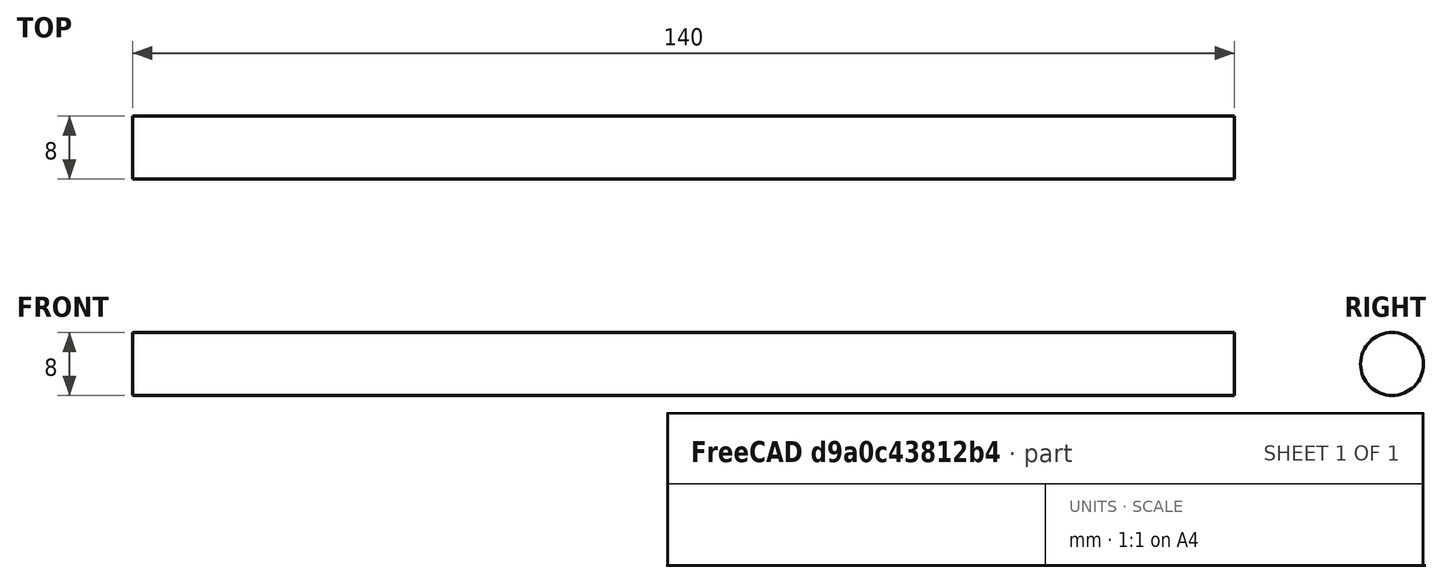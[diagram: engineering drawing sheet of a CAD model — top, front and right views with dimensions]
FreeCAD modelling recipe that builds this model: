
FCSTD DOCUMENT  (FreeCAD 0.15R4671 (Git))
Label: axe 2
License: All rights reserved
LicenseURL: http://fr.wikipedia.org/wiki/<copyright redacted>
objects: Sketcher::SketchObject×1, PartDesign::Revolution×1
note: 3 computed .brp shape members not serialized (recipe doc carries the construction recipe); baked Part::Feature solids carry a one-line shape summary decoded from their .brp

FEATURE [Sketcher::SketchObject] Sketch
  sketch-geometry (4):
    g0: LineSegment StartX=0 StartY=0 StartZ=0 EndX=-140 EndY=0 EndZ=0
    g1: LineSegment StartX=-140 StartY=0 StartZ=0 EndX=-140 EndY=4 EndZ=0
    g2: LineSegment StartX=-140 StartY=4 StartZ=0 EndX=0 EndY=4 EndZ=0
    g3: LineSegment StartX=0 StartY=4 StartZ=0 EndX=0 EndY=0 EndZ=0
  constraints (11):
    c: Coincident(g0,g1)
    c: Coincident(g1,g2)
    c: Coincident(g2,g3)
    c: Coincident(g3,g0)
    c: Horizontal(g0)
    c: Horizontal(g2)
    c: Vertical(g1)
    c: Vertical(g3)
    c: Coincident(g0,g-1)
    c: Distance(g3) = 4
    c: Distance(g2) = 140
FEATURE [PartDesign::Revolution] Revolution
  Angle = 360
  Axis = (1,0,0)
  Base = (0,0,0)
  ReferenceAxis = -> Sketch [H_Axis]
  Sketch = -> Sketch
